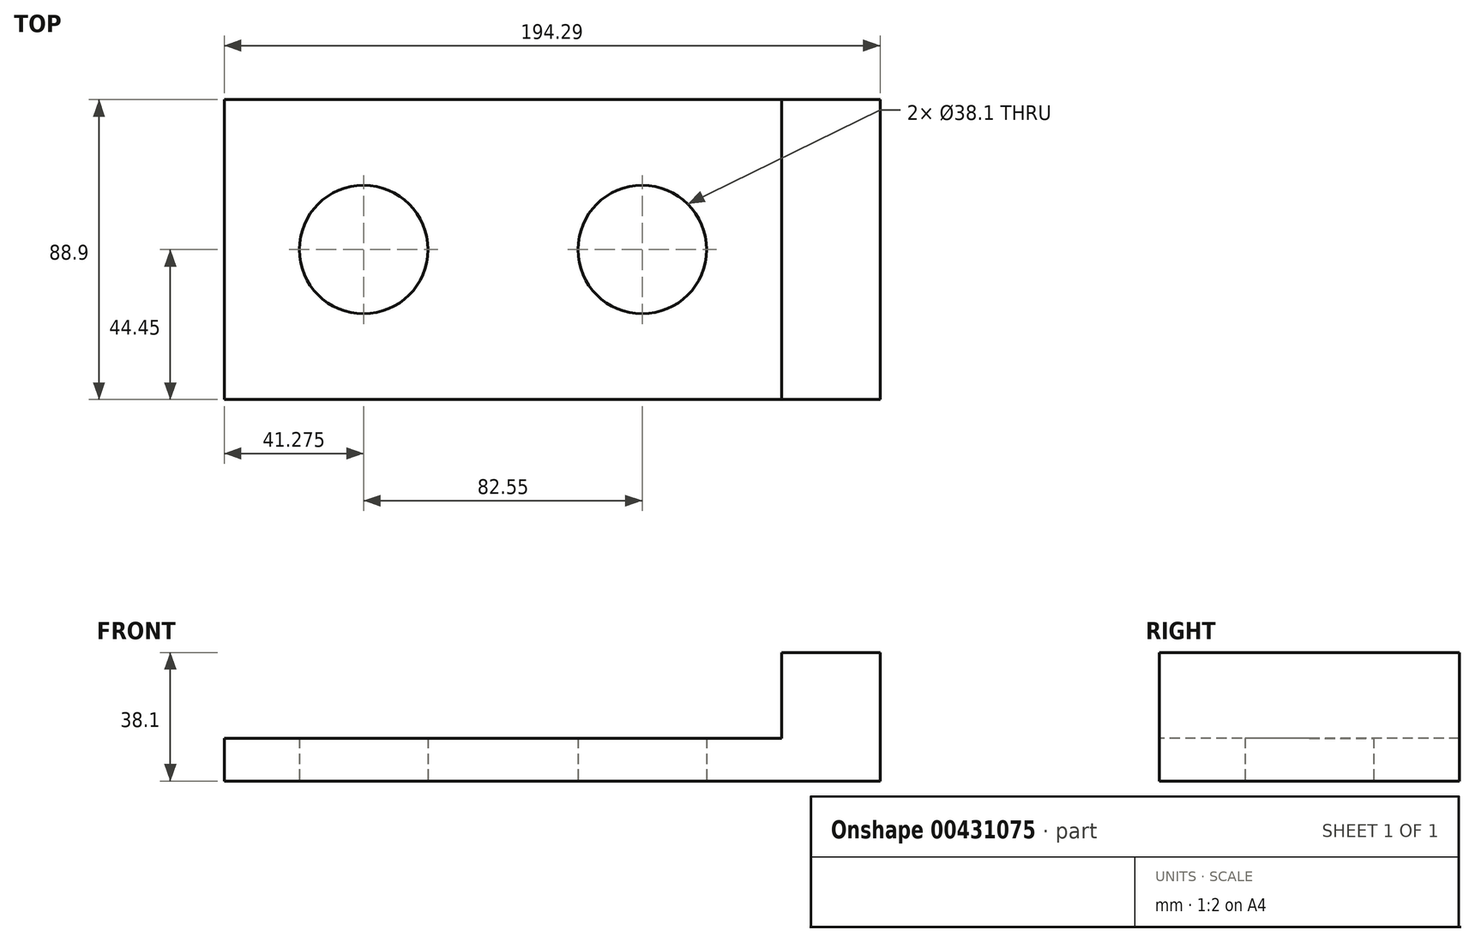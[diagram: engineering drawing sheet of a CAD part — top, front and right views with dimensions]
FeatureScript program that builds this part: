
annotation { "Feature Type Name" : "Feature", "Feature Type Description" : "" }
export const myFeature = defineFeature(function(context is Context, id is Id, definition is map)
    precondition{}
    {
        {
            var Q0;
            Q0=qCreatedBy(makeId("Top.planeOp"),FACE);
            var sketch = newSketch(context, id + "F0", { "sketchPlane" : qUnion([Q0])});
            skLineSegment(sketch, "E0.bottom", {"start": v(0, 0) * mm, "end": v(165.1, 0) * mm});
            skLineSegment(sketch, "E0.top", {"start": v(0, -88.9) * mm, "end": v(165.1, -88.9) * mm});
            skLineSegment(sketch, "E0.left", {"start": v(0, 0) * mm, "end": v(0, -88.9) * mm});
            skLineSegment(sketch, "E0.right", {"start": v(165.1, 0) * mm, "end": v(165.1, -88.9) * mm});
            skLineSegment(sketch, "E1", {"start": v(82.55, -88.9) * mm, "end": v(82.55, 0) * mm});
            skSolve(sketch);
        }
        {
            var Q0;
            Q0=makeQuery(id+"F0.imprint","IMPRINT",FACE,{"disambiguationData":[TD([[makeQuery(id+"F0.imprint","IMPRINT",EDGE,{"derivedFrom":sQuery(id+"F0.wireOp",EDGE,"E0.bottom")}),-1.0]])]});
            extrude(context, id + "F1", {"entities" : qUnion([Q0]), "depth" : 12.7 * mm});
        }
        {
            var Q0;
            Q0=qCreatedBy(makeId("Top.planeOp"),FACE);
            var sketch = newSketch(context, id + "F2", { "sketchPlane" : qUnion([Q0])});
            skCircle(sketch, "E2", {"center": v(123.83, -44.45) * mm, "radius": 19.05 * mm});
            skCircle(sketch, "E3", {"center": v(41.27, -44.45) * mm, "radius": 19.05 * mm});
            skSolve(sketch);
        }
        {
            var Q0;
            Q0=sQuery(id+"F2.wireOp",VERTEX,"E2.center");
            var Q1;
            Q1=sQuery(id+"F2.wireOp",VERTEX,"E3.center");
            var Q2;
            Q2=makeQuery(id+"F1.opExtrude","SWEPT_BODY",BODY,{"disambiguationData":[OSD([sQuery(id+"F0.wireOp",EDGE,"E0.bottom"),sQuery(id+"F0.wireOp",EDGE,"E0.top"),sQuery(id+"F0.wireOp",EDGE,"E0.left"),sQuery(id+"F0.wireOp",EDGE,"E0.right")])]});
            hole(context, id + "F3", {"style" : HoleStyle.SIMPLE, "endStyle" : HoleEndStyle.THROUGH, "oppositeDirection" : true, "holeDiameter" : 38.1 * mm, "isTappedThrough" : true, "tappedDepth" : 12.7 * mm, "tapClearance" : 3, "locations" : qUnion([Q0, Q1]), "scope" : qUnion([Q2])});
        }
        {
            var Q0;
            Q0=makeQuery(id+"F1.opExtrude","CAP_FACE",FACE,{"disambiguationData":[OSD([sQuery(id+"F0.wireOp",EDGE,"E0.bottom"),sQuery(id+"F0.wireOp",EDGE,"E0.top"),sQuery(id+"F0.wireOp",EDGE,"E0.left"),sQuery(id+"F0.wireOp",EDGE,"E0.right")])],"isStart":true});
            var sketch = newSketch(context, id + "F4", { "sketchPlane" : qUnion([Q0])});
            skLineSegment(sketch, "E4", {"start": v(165.1, 88.9) * mm, "end": v(165.1, 0) * mm});
            skLineSegment(sketch, "E5", {"start": v(165.1, 0) * mm, "end": v(170.67, 0) * mm});
            skLineSegment(sketch, "E6", {"start": v(170.67, 0) * mm, "end": v(170.67, 88.9) * mm});
            skLineSegment(sketch, "E7", {"start": v(170.67, 88.9) * mm, "end": v(165.1, 88.9) * mm});
            skSolve(sketch);
        }
        {
            var Q0;
            Q0=makeQuery(id+"F4.imprint","IMPRINT",FACE,{"disambiguationData":[TD([[makeQuery(id+"F4.imprint","IMPRINT",EDGE,{"derivedFrom":sQuery(id+"F4.wireOp",EDGE,"E4")}),-1.0]])]});
            extrude(context, id + "F5", {"entities" : qUnion([Q0]), "operationType" : NewBodyOperationType.ADD, "oppositeDirection" : true, "depth" : 38.1 * mm});
        }
        {
            var Q0;
            Q0=makeQuery(id+"F5.opExtrude","SWEPT_FACE",FACE,{"disambiguationData":[OSD([sQuery(id+"F4.wireOp",EDGE,"E6")])]});
            var sketch = newSketch(context, id + "F6", { "sketchPlane" : qUnion([Q0])});
            skSolve(sketch);
        }
        {
            var Q0;
            {var subQ0=sQuery(id+"F4.wireOp",EDGE,"E6");Q0=makeQuery(id+"F6.imprint","IMPRINT",FACE,{"disambiguationData":[TD([[makeQuery(id+"F6.imprint","IMPRINT",EDGE,{"derivedFrom":makeQuery(id+"F5.opExtrude","CAP_EDGE",EDGE,{"disambiguationData":[OSD([subQ0])],"isStart":true})}),-1.0]])]});}
            extrude(context, id + "F7", {"entities" : qUnion([Q0]), "operationType" : NewBodyOperationType.ADD, "depth" : 23.62 * mm});
        }
    });
